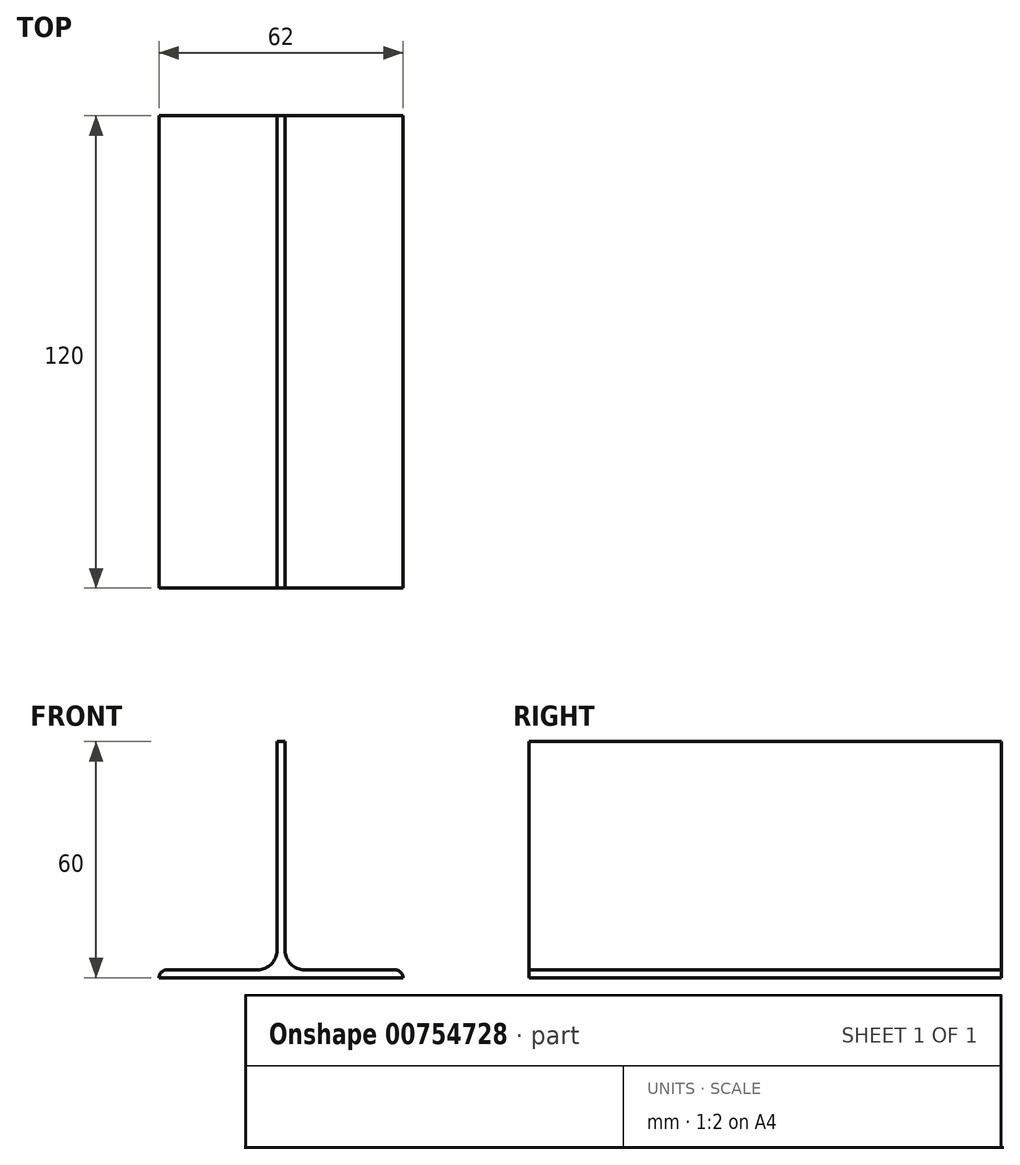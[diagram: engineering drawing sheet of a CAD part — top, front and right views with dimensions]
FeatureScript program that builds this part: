
annotation { "Feature Type Name" : "Feature", "Feature Type Description" : "" }
export const myFeature = defineFeature(function(context is Context, id is Id, definition is map)
    precondition{}
    {
        {
            var Q0;
            Q0=qCreatedBy(makeId("Front.planeOp"),FACE);
            var sketch = newSketch(context, id + "F0", { "sketchPlane" : qUnion([Q0])});
            skLineSegment(sketch, "E0", {"start": v(0, 0) * mm, "end": v(0, 62.58) * mm, "construction": true});
            skLineSegment(sketch, "E1", {"start": v(0, 60) * mm, "end": v(-1, 60) * mm});
            skLineSegment(sketch, "E2", {"start": v(-1, 60) * mm, "end": v(-1, 2) * mm});
            skLineSegment(sketch, "E3", {"start": v(-1, 2) * mm, "end": v(-31, 2) * mm});
            skLineSegment(sketch, "E4", {"start": v(-31, 2) * mm, "end": v(-31, 0) * mm});
            skLineSegment(sketch, "E5", {"start": v(-31, 0) * mm, "end": v(0, 0) * mm});
            skLineSegment(sketch, "E6.MirrorCS", {"start": v(0, 60) * mm, "end": v(1, 60) * mm});
            skLineSegment(sketch, "E7.MirrorCS", {"start": v(1, 60) * mm, "end": v(1, 2) * mm});
            skLineSegment(sketch, "E8.MirrorCS", {"start": v(1, 2) * mm, "end": v(31, 2) * mm});
            skLineSegment(sketch, "E9.MirrorCS", {"start": v(31, 2) * mm, "end": v(31, 0) * mm});
            skLineSegment(sketch, "E10.MirrorCS", {"start": v(31, 0) * mm, "end": v(0, 0) * mm});
            skSolve(sketch);
        }
        {
            var Q0;
            Q0 = qSketchRegion(id + "F0", true);
            extrude(context, id + "F1", {"entities" : qUnion([Q0]), "depth" : 120 * mm, "offsetDistance" : 25 * mm});
        }
        {
            var Q0;
            Q0=makeQuery(id+"F1.opExtrude","SWEPT_EDGE",EDGE,{"disambiguationData":[OSD([sQuery(id+"F0.wireOp",EDGE,"E2"),sQuery(id+"F0.wireOp",EDGE,"E3")])]});
            var Q1;
            Q1=makeQuery(id+"F1.opExtrude","SWEPT_EDGE",EDGE,{"disambiguationData":[OSD([sQuery(id+"F0.wireOp",EDGE,"E7.MirrorCS"),sQuery(id+"F0.wireOp",EDGE,"E8.MirrorCS")])]});
            fillet(context, id + "F2", {"entities" : qUnion([Q0, Q1]), "radius" : 5 * mm, "tangentPropagation" : true, "allowEdgeOverflow" : false});
        }
        {
            var Q0;
            Q0=makeQuery(id+"F1.opExtrude","SWEPT_EDGE",EDGE,{"disambiguationData":[OSD([sQuery(id+"F0.wireOp",EDGE,"E8.MirrorCS"),sQuery(id+"F0.wireOp",EDGE,"E9.MirrorCS")])]});
            var Q1;
            Q1=makeQuery(id+"F1.opExtrude","SWEPT_EDGE",EDGE,{"disambiguationData":[OSD([sQuery(id+"F0.wireOp",EDGE,"E3"),sQuery(id+"F0.wireOp",EDGE,"E4")])]});
            fillet(context, id + "F3", {"entities" : qUnion([Q0, Q1]), "radius" : 2 * mm, "tangentPropagation" : true, "allowEdgeOverflow" : false});
        }
    });
